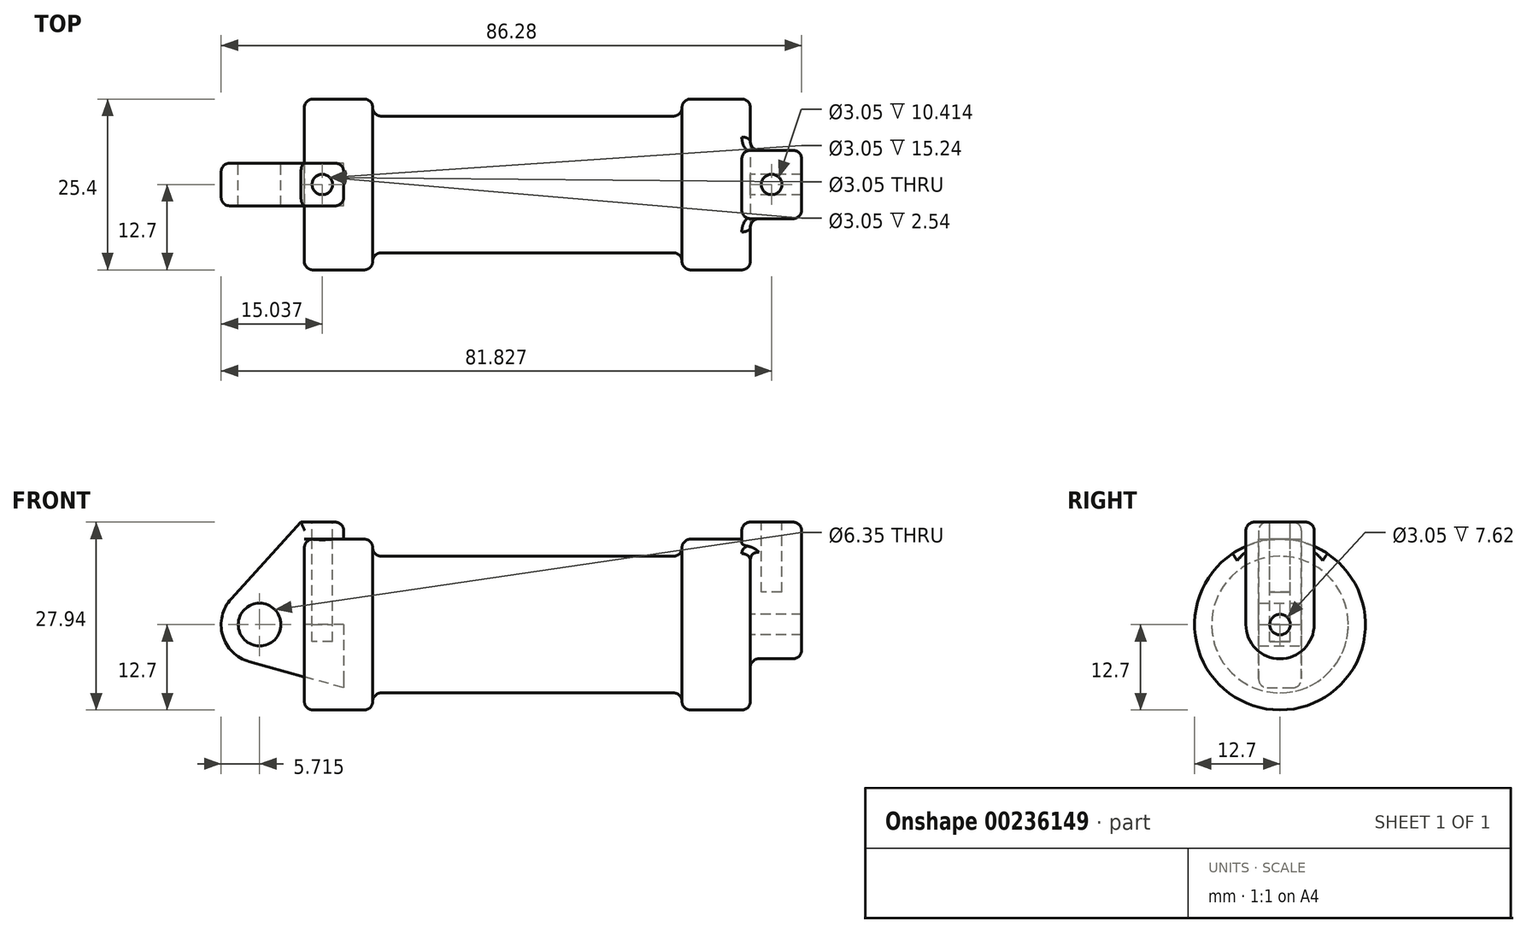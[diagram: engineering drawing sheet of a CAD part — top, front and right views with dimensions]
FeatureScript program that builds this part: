
annotation { "Feature Type Name" : "Feature", "Feature Type Description" : "" }
export const myFeature = defineFeature(function(context is Context, id is Id, definition is map)
    precondition{}
    {
        {
            var Q0;
            Q0=qCreatedBy(makeId("Front.planeOp"),FACE);
            var sketch = newSketch(context, id + "F0", { "sketchPlane" : qUnion([Q0])});
            skLineSegment(sketch, "E0", {"start": v(0, 0) * mm, "end": v(0, 12.7) * mm});
            skLineSegment(sketch, "E1", {"start": v(0, 12.7) * mm, "end": v(10.16, 12.7) * mm});
            skLineSegment(sketch, "E2", {"start": v(10.16, 12.7) * mm, "end": v(10.16, 10.16) * mm});
            skLineSegment(sketch, "E3", {"start": v(10.16, 10.16) * mm, "end": v(56.13, 10.16) * mm});
            skLineSegment(sketch, "E4", {"start": v(56.13, 10.16) * mm, "end": v(56.13, 12.7) * mm});
            skLineSegment(sketch, "E5", {"start": v(56.13, 12.7) * mm, "end": v(66.3, 12.7) * mm});
            skLineSegment(sketch, "E6", {"start": v(66.3, 12.7) * mm, "end": v(66.3, 0) * mm});
            skLineSegment(sketch, "E7", {"start": v(66.3, 0) * mm, "end": v(0, 0) * mm});
            skLineSegment(sketch, "E8", {"start": v(5.84, 15.24) * mm, "end": v(-0.5, 15.24) * mm});
            skLineSegment(sketch, "E9", {"start": v(-0.5, 15.24) * mm, "end": v(-10.88, 3.85) * mm});
            skLineSegment(sketch, "E10", {"start": v(0, 0) * mm, "end": v(-6.65, 0) * mm});
            skCircle(sketch, "E11", {"center": v(-6.65, 0) * mm, "radius": 5.72 * mm});
            skCircle(sketch, "E12", {"center": v(-6.65, 0) * mm, "radius": 3.18 * mm});
            skLineSegment(sketch, "E13", {"start": v(5.84, 15.24) * mm, "end": v(5.84, -9.4) * mm});
            skLineSegment(sketch, "E14", {"start": v(5.84, -9.4) * mm, "end": v(-8.18, -5.5) * mm});
            skSolve(sketch);
        }
        {
            var Q0;
            {var subQ3=sQuery(id+"F0.wireOp",EDGE,"E0");Q0=makeQuery(id+"F0.imprint","IMPRINT",FACE,{"disambiguationData":[TD([[makeQuery(id+"F0.imprint","IMPRINT",EDGE,{"derivedFrom":subQ3}),1.0]])]});}
            var Q1;
            {var subQ4=sQuery(id+"F0.wireOp",EDGE,"E12");Q1=makeQuery(id+"F0.imprint","IMPRINT",FACE,{"disambiguationData":[TD([[makeQuery(id+"F0.imprint","IMPRINT",EDGE,{"derivedFrom":subQ4}),-1.0]])]});}
            var Q2;
            {var subQ0=sQuery(id+"F0.wireOp",EDGE,"E14");Q2=makeQuery(id+"F0.imprint","IMPRINT",FACE,{"disambiguationData":[TD([[makeQuery(id+"F0.imprint","IMPRINT",EDGE,{"derivedFrom":subQ0}),-1.0]])]});}
            extrude(context, id + "F1", {"entities" : qUnion([Q0, Q1, Q2]), "endBound" : BoundingType.SYMMETRIC, "depth" : 6.35 * mm, "hasSecondDirection" : true, "secondDirectionOppositeDirection" : true, "secondDirectionDepth" : 6.35 * mm});
        }
        {
            var Q0;
            {var subQ0=sQuery(id+"F0.wireOp",EDGE,"E2");Q0=makeQuery(id+"F0.imprint","IMPRINT",FACE,{"disambiguationData":[TD([[makeQuery(id+"F0.imprint","IMPRINT",EDGE,{"derivedFrom":subQ0}),-1.0]])]});}
            var Q1;
            {var subQ0=sQuery(id+"F0.wireOp",EDGE,"E0");Q1=makeQuery(id+"F0.imprint","IMPRINT",FACE,{"disambiguationData":[TD([[makeQuery(id+"F0.imprint","IMPRINT",EDGE,{"derivedFrom":subQ0}),-1.0]])]});}
            var Q2;
            Q2=sQuery(id+"F0.wireOp",EDGE,"E7");
            revolve(context, id + "F2", {"entities" : qUnion([Q0, Q1]), "axis" : qUnion([Q2]), "revolveType" : RevolveType.FULL});
        }
        {
            var Q0;
            Q0=makeQuery(id+"F2.opRevolve","SWEPT_FACE",FACE,{"disambiguationData":[OSD([sQuery(id+"F0.wireOp",EDGE,"E6")])]});
            var sketch = newSketch(context, id + "F3", { "sketchPlane" : qUnion([Q0])});
            skCircle(sketch, "E15", {"center": v(0, 0) * mm, "radius": 1.52 * mm});
            skCircle(sketch, "E16", {"center": v(0, 0) * mm, "radius": 5.08 * mm});
            skLineSegment(sketch, "E17", {"start": v(-5.08, 0) * mm, "end": v(-5.08, 15.24) * mm});
            skLineSegment(sketch, "E18", {"start": v(-5.08, 15.24) * mm, "end": v(5.08, 15.24) * mm});
            skLineSegment(sketch, "E19", {"start": v(5.08, 15.24) * mm, "end": v(5.08, 0) * mm});
            skSolve(sketch);
        }
        {
            var Q0;
            Q0 = qSketchRegion(id + "F3", true);
            extrude(context, id + "F4", {"entities" : qUnion([Q0]), "operationType" : NewBodyOperationType.ADD, "depth" : 7.62 * mm, "hasSecondDirection" : true, "secondDirectionOppositeDirection" : true, "secondDirectionDepth" : 1.27 * mm});
        }
        {
            var Q0;
            Q0=makeQuery(id+"F1.opExtrude","SWEPT_FACE",FACE,{"disambiguationData":[OSD([sQuery(id+"F0.wireOp",EDGE,"E8")])]});
            var sketch = newSketch(context, id + "F5", { "sketchPlane" : qUnion([Q0])});
            skCircle(sketch, "E20", {"center": v(2.67, 0) * mm, "radius": 1.52 * mm});
            skCircle(sketch, "E21", {"center": v(69.46, 0) * mm, "radius": 1.52 * mm});
            skPoint(sketch, "E22.orphan", {"position": v(65, 0) * mm});
            skPoint(sketch, "E23.end.orphan", {"position": v(73.92, 0) * mm});
            skPoint(sketch, "E24.orphan", {"position": v(2.67, 3.18) * mm});
            skPoint(sketch, "E25.end.orphan", {"position": v(2.67, -3.18) * mm});
            skSolve(sketch);
        }
        {
            var Q0;
            Q0=makeQuery(id+"F5.imprint","IMPRINT",FACE,{"disambiguationData":[TD([[makeQuery(id+"F5.imprint","IMPRINT",EDGE,{"derivedFrom":sQuery(id+"F5.wireOp",EDGE,"E21")}),1.0]])]});
            extrude(context, id + "F6", {"entities" : qUnion([Q0]), "operationType" : NewBodyOperationType.REMOVE, "oppositeDirection" : true, "depth" : 10.4 * mm});
        }
        {
            var Q0;
            Q0=makeQuery(id+"F5.imprint","IMPRINT",FACE,{"disambiguationData":[TD([[makeQuery(id+"F5.imprint","IMPRINT",EDGE,{"derivedFrom":sQuery(id+"F5.wireOp",EDGE,"E20")}),1.0]])]});
            extrude(context, id + "F7", {"entities" : qUnion([Q0]), "operationType" : NewBodyOperationType.REMOVE, "oppositeDirection" : true, "depth" : 17.78 * mm});
        }
        {
            var Q0;
            Q0=makeQuery(id+"F2.opRevolve","SWEPT_FACE",FACE,{"disambiguationData":[OSD([sQuery(id+"F0.wireOp",EDGE,"E3")])]});
            var Q1;
            Q1=makeQuery(id+"F2.opRevolve","SWEPT_EDGE",EDGE,{"disambiguationData":[OSD([sQuery(id+"F0.wireOp",EDGE,"E4"),sQuery(id+"F0.wireOp",EDGE,"E5")])]});
            var Q2;
            Q2=makeQuery(id+"F2.opRevolve","SWEPT_EDGE",EDGE,{"disambiguationData":[OSD([sQuery(id+"F0.wireOp",EDGE,"E1"),sQuery(id+"F0.wireOp",EDGE,"E2")])]});
            fillet(context, id + "F8", {"entities" : qUnion([Q0, Q1, Q2]), "radius" : 1.27 * mm, "tangentPropagation" : true, "allowEdgeOverflow" : false});
        }
        {
            var Q0;
            Q0=makeQuery(id+"F4.opExtrude","SWEPT_EDGE",EDGE,{"disambiguationData":[OSD([sQuery(id+"F3.wireOp",EDGE,"E18"),sQuery(id+"F3.wireOp",EDGE,"E19")])]});
            var Q1;
            Q1=makeQuery(id+"F4.opExtrude","CAP_EDGE",EDGE,{"disambiguationData":[OSD([sQuery(id+"F3.wireOp",EDGE,"E18")])],"isStart":true});
            var Q2;
            Q2=makeQuery(id+"F4.opExtrude","CAP_EDGE",EDGE,{"disambiguationData":[OSD([sQuery(id+"F3.wireOp",EDGE,"E19")])],"isStart":true});
            var Q3;
            Q3=makeQuery(id+"F4.opExtrude","CAP_EDGE",EDGE,{"disambiguationData":[OSD([sQuery(id+"F3.wireOp",EDGE,"E17")])],"isStart":true});
            var Q4;
            Q4=makeQuery(id+"F4.opExtrude","SWEPT_EDGE",EDGE,{"disambiguationData":[OSD([sQuery(id+"F3.wireOp",EDGE,"E17"),sQuery(id+"F3.wireOp",EDGE,"E18")])]});
            var Q5;
            Q5=makeQuery(id+"F4.opExtrude","CAP_EDGE",EDGE,{"disambiguationData":[OSD([sQuery(id+"F3.wireOp",EDGE,"E18")])],"isStart":false});
            var Q6;
            Q6=makeQuery(id+"F4.opExtrude","CAP_EDGE",EDGE,{"disambiguationData":[OSD([sQuery(id+"F3.wireOp",EDGE,"E17")])],"isStart":false});
            var Q7;
            Q7=makeQuery(id+"F1.opExtrude","CAP_EDGE",EDGE,{"disambiguationData":[OSD([sQuery(id+"F0.wireOp",EDGE,"E8")])],"isStart":false});
            var Q8;
            {var subQ0=sQuery(id+"F0.wireOp",EDGE,"E13");Q8=makeQuery(id+"F1.opExtrude","CAP_EDGE",EDGE,{"disambiguationData":[OSD([subQ0]),TDD([makeQuery(id+"F0.imprint","IMPRINT",EDGE,{"disambiguationData":[TD([[makeQuery(id+"F0.imprint","INTERSECT",VERTEX,{"derivedFrom":[sQuery(id+"F0.wireOp",EDGE,"E8"),subQ0]}),-1.0]])],"derivedFrom":subQ0})])],"isStart":false});}
            var Q9;
            Q9=makeQuery(id+"F1.opExtrude","SWEPT_EDGE",EDGE,{"disambiguationData":[OSD([sQuery(id+"F0.wireOp",EDGE,"E8"),sQuery(id+"F0.wireOp",EDGE,"E13")])]});
            var Q10;
            Q10=makeQuery(id+"F1.opExtrude","CAP_EDGE",EDGE,{"disambiguationData":[OSD([sQuery(id+"F0.wireOp",EDGE,"E8")])],"isStart":true});
            var Q11;
            {var subQ0=sQuery(id+"F0.wireOp",EDGE,"E13");Q11=makeQuery(id+"F1.opExtrude","CAP_EDGE",EDGE,{"disambiguationData":[OSD([subQ0]),TDD([makeQuery(id+"F0.imprint","IMPRINT",EDGE,{"disambiguationData":[TD([[makeQuery(id+"F0.imprint","INTERSECT",VERTEX,{"derivedFrom":[sQuery(id+"F0.wireOp",EDGE,"E8"),subQ0]}),-1.0]])],"derivedFrom":subQ0})])],"isStart":true});}
            var Q12;
            Q12=makeQuery(id+"F1.opExtrude","CAP_EDGE",EDGE,{"disambiguationData":[OSD([sQuery(id+"F0.wireOp",EDGE,"E9")])],"isStart":true});
            var Q13;
            Q13=makeQuery(id+"F1.opExtrude","CAP_EDGE",EDGE,{"disambiguationData":[OSD([sQuery(id+"F0.wireOp",EDGE,"E9")])],"isStart":false});
            var Q14;
            Q14=makeQuery(id+"F1.opExtrude","CAP_EDGE",EDGE,{"disambiguationData":[OSD([sQuery(id+"F0.wireOp",EDGE,"E11")])],"isStart":false});
            var Q15;
            Q15=makeQuery(id+"F1.opExtrude","CAP_EDGE",EDGE,{"disambiguationData":[OSD([sQuery(id+"F0.wireOp",EDGE,"E14")])],"isStart":false});
            var Q16;
            Q16=makeQuery(id+"F1.opExtrude","CAP_EDGE",EDGE,{"disambiguationData":[OSD([sQuery(id+"F0.wireOp",EDGE,"E11")])],"isStart":true});
            var Q17;
            Q17=makeQuery(id+"F1.opExtrude","CAP_EDGE",EDGE,{"disambiguationData":[OSD([sQuery(id+"F0.wireOp",EDGE,"E14")])],"isStart":true});
            fillet(context, id + "F9", {"entities" : qUnion([Q0, Q1, Q2, Q3, Q4, Q5, Q6, Q7, Q8, Q9, Q10, Q11, Q12, Q13, Q14, Q15, Q16, Q17]), "radius" : 1.27 * mm, "tangentPropagation" : true, "allowEdgeOverflow" : false});
        }
        {
            var Q0;
            Q0=makeQuery(id+"F4.boolean.opBoolean","INTERSECT",EDGE,{"derivedFrom":[makeQuery(id+"F2.opRevolve","SWEPT_FACE",FACE,{"disambiguationData":[OSD([sQuery(id+"F0.wireOp",EDGE,"E6")])]}),makeQuery(id+"F4.opExtrude","SWEPT_FACE",FACE,{"disambiguationData":[OSD([sQuery(id+"F3.wireOp",EDGE,"E17")])]})]});
            var Q1;
            Q1=makeQuery(id+"F4.boolean.opBoolean","INTERSECT",EDGE,{"derivedFrom":[makeQuery(id+"F2.opRevolve","SWEPT_FACE",FACE,{"disambiguationData":[OSD([sQuery(id+"F0.wireOp",EDGE,"E6")])]}),makeQuery(id+"F4.opExtrude","SWEPT_FACE",FACE,{"disambiguationData":[OSD([sQuery(id+"F3.wireOp",EDGE,"E16")])]})]});
            fillet(context, id + "F10", {"entities" : qUnion([Q0, Q1]), "radius" : 1.27 * mm, "tangentPropagation" : true, "allowEdgeOverflow" : false});
        }
        {
            var Q0;
            Q0=makeQuery(id+"F2.opRevolve","SWEPT_EDGE",EDGE,{"disambiguationData":[OSD([sQuery(id+"F0.wireOp",EDGE,"E5"),sQuery(id+"F0.wireOp",EDGE,"E6")])]});
            var Q1;
            Q1=makeQuery(id+"F2.opRevolve","SWEPT_EDGE",EDGE,{"disambiguationData":[OSD([sQuery(id+"F0.wireOp",EDGE,"E0"),sQuery(id+"F0.wireOp",EDGE,"E1")])]});
            fillet(context, id + "F11", {"entities" : qUnion([Q0, Q1]), "radius" : 1.27 * mm, "tangentPropagation" : true, "allowEdgeOverflow" : false});
        }
    });
